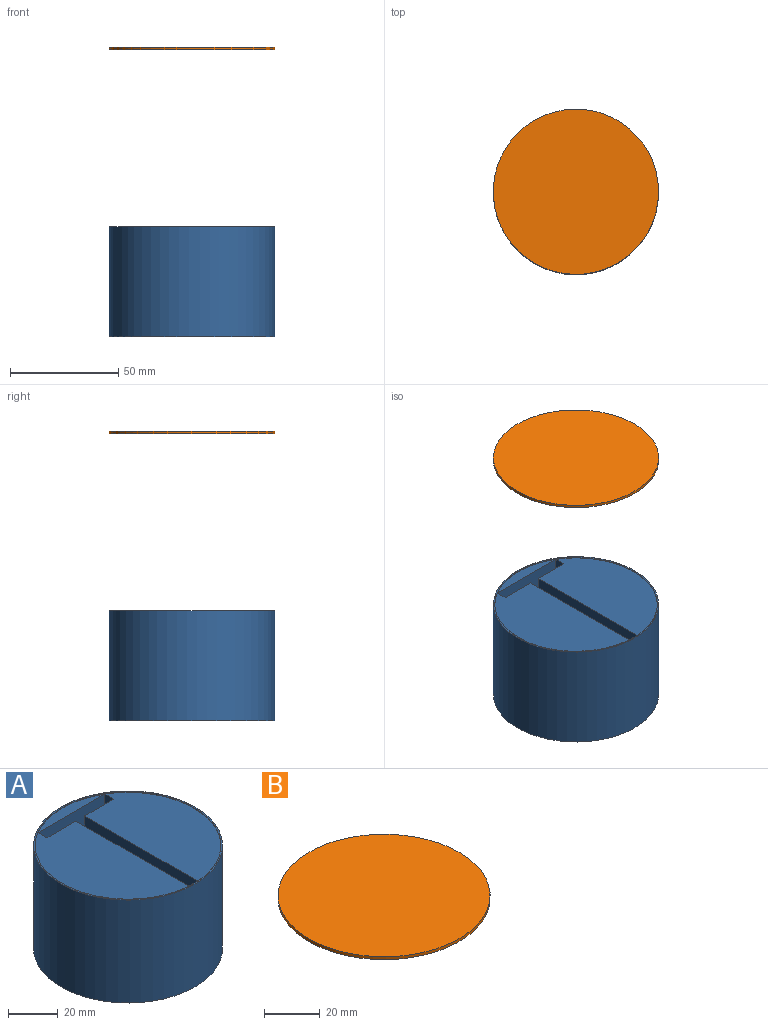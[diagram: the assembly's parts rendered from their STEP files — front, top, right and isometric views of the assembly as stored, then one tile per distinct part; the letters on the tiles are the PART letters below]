
ASSEMBLY  parts=2 mates=1
PART A: 17 faces, bbox 76.2x76.2x50.8 mm
  f0: plane 38.1x5.2mm, normal (0,0,1), area 134.2mm2, adj f7,f8
  f1: plane 69.64x34.93mm, normal (0,0,1), area 1876.8mm2, adj f7,f9,f10,f11
  f2: plane 5.08x0.09mm, normal (0,0,1), area 0.3mm2, adj f7,f12
  f3: plane 69.64x34.93mm, normal (0,0,1), area 1876.8mm2, adj f7,f13,f14,f15
  f4: cylinder r=38.1mm len=76.2mm, axis (0,0,-1), area 12161mm2, adj f5,f6
  f5: plane 76.2x76.2mm, normal (0,0,1), area 150.7mm2, adj f4,f7
  f6: plane 76.2x76.2mm, normal (0,0,-1), area 4560.4mm2, adj f4
  f7: cylinder r=37.46mm len=74.93mm, axis (0,0,1), area 59.8mm2, adj f0,f1,f2,f3,f5
  f8: plane 50.29x38.1mm, normal (0,-1,0), area 1916.1mm2, adj f0,f9,f15,f16
  f9: plane 50.29x5.08mm, normal (1,0,0), area 255.5mm2, adj f1,f8,f10,f16
  f10: plane 50.29x16.51mm, normal (0,1,0), area 830.3mm2, adj f1,f9,f11,f16
  f11: plane 64.56x50.29mm, normal (1,0,0), area 3246.8mm2, adj f1,f10,f12,f16
  f12: plane 50.29x5.08mm, normal (0,1,0), area 255.5mm2, adj f2,f11,f13,f16
  f13: plane 64.56x50.29mm, normal (-1,0,0), area 3246.8mm2, adj f3,f12,f14,f16
  f14: plane 50.29x16.51mm, normal (0,1,0), area 830.3mm2, adj f3,f13,f15,f16
  f15: plane 50.29x5.08mm, normal (-1,0,0), area 255.5mm2, adj f3,f8,f14,f16
  f16: plane 69.64x38.1mm, normal (0,0,1), area 521.5mm2, adj f8,f9,f10,f11,f12,f13,f14,f15
PART B: 3 faces, bbox 76.2x76.2x1.3 mm
  f0: cylinder r=38.1mm len=76.2mm, axis (0,0,-1), area 304mm2, adj f1,f2
  f1: plane 76.2x76.2mm, normal (0,0,1), area 4560.4mm2, adj f0
  f2: plane 76.2x76.2mm, normal (0,0,-1), area 4560.4mm2, adj f0
PLACE A t=(-45.45,-1.37,-82.74)mm
PLACE B t=(-45.45,-1.37,49.63)mm
MATE cylindrical A.f4 <-> B.f0  axis (0,0,-1) through (-45.45,-1.37,-57.34)mm
